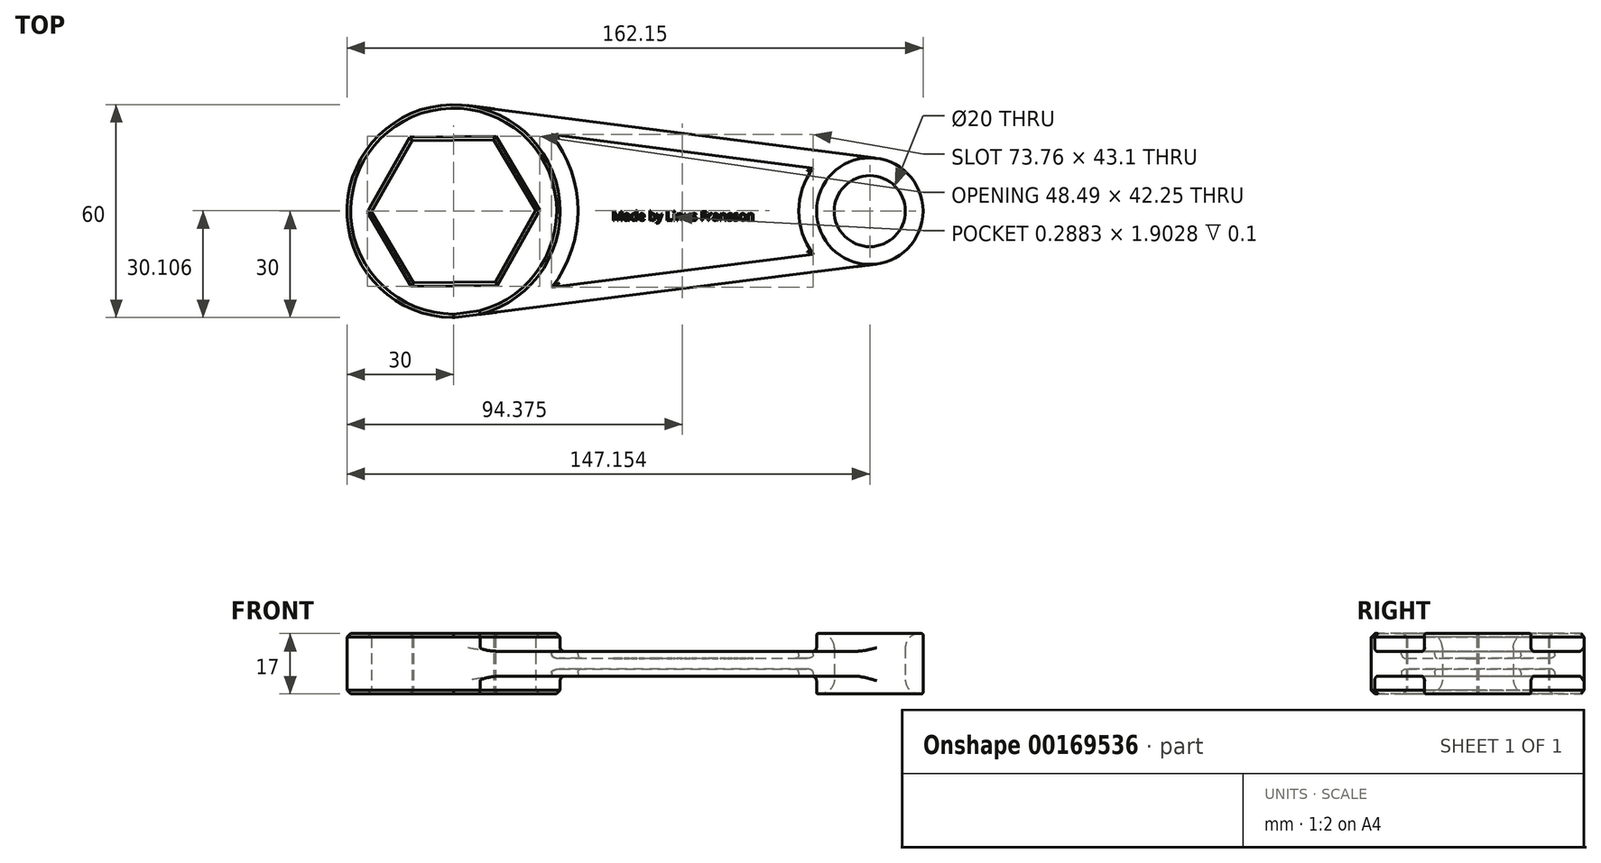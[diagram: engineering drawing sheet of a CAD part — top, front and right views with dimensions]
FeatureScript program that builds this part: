
annotation { "Feature Type Name" : "Feature", "Feature Type Description" : "" }
export const myFeature = defineFeature(function(context is Context, id is Id, definition is map)
    precondition{}
    {
        {
            var Q0;
            Q0=qCreatedBy(makeId("Top.planeOp"),FACE);
            var sketch = newSketch(context, id + "F0", { "sketchPlane" : qUnion([Q0])});
            skCircle(sketch, "E0", {"center": v(0, 0) * mm, "radius": 30 * mm});
            skCircle(sketch, "E1", {"center": v(117.15, 0) * mm, "radius": 15 * mm});
            skCircle(sketch, "E2.cCircle", {"center": v(0, 0) * mm, "radius": 20 * mm, "construction": true});
            skLineSegment(sketch, "E2.0", {"start": v(23.1, 0.24) * mm, "end": v(11.76, -19.88) * mm});
            skLineSegment(sketch, "E2.1", {"start": v(11.76, -19.88) * mm, "end": v(-11.34, -20.12) * mm});
            skLineSegment(sketch, "E2.2", {"start": v(-11.34, -20.12) * mm, "end": v(-23.1, -0.24) * mm});
            skLineSegment(sketch, "E2.3", {"start": v(-23.1, -0.24) * mm, "end": v(-11.76, 19.88) * mm});
            skLineSegment(sketch, "E2.4", {"start": v(-11.76, 19.88) * mm, "end": v(11.34, 20.12) * mm});
            skLineSegment(sketch, "E2.5", {"start": v(11.34, 20.12) * mm, "end": v(23.1, 0.24) * mm});
            skPoint(sketch, "E2.0.midPoint", {"position": v(17.42, -9.82) * mm});
            skCircle(sketch, "E3", {"center": v(117.15, 0) * mm, "radius": 10 * mm});
            skLineSegment(sketch, "E4", {"start": v(119.01, 14.88) * mm, "end": v(0, 30.25) * mm});
            skLineSegment(sketch, "E5", {"start": v(0, -30) * mm, "end": v(119.04, -14.88) * mm});
            skSolve(sketch);
        }
        {
            var Q0;
            {var subQ0=sQuery(id+"F0.wireOp",EDGE,"E4");var subQ1=sQuery(id+"F0.wireOp",EDGE,"E0");var subQ2=makeQuery(id+"F0.imprint","INTERSECT",VERTEX,{"derivedFrom":[subQ1,subQ0]});Q0=makeQuery(id+"F0.imprint","IMPRINT",FACE,{"disambiguationData":[TD([[makeQuery(id+"F0.imprint","IMPRINT",EDGE,{"disambiguationData":[TD([[subQ2,1.0]])],"derivedFrom":subQ1}),-1.0]])]});}
            var Q1;
            Q1=makeQuery(id+"F0.imprint","IMPRINT",FACE,{"disambiguationData":[TD([[makeQuery(id+"F0.imprint","IMPRINT",EDGE,{"derivedFrom":sQuery(id+"F0.wireOp",EDGE,"E2.0")}),1.0]])]});
            var Q2;
            Q2=makeQuery(id+"F0.imprint","IMPRINT",FACE,{"disambiguationData":[TD([[makeQuery(id+"F0.imprint","IMPRINT",EDGE,{"derivedFrom":sQuery(id+"F0.wireOp",EDGE,"E3")}),-1.0]])]});
            extrude(context, id + "F1", {"entities" : qUnion([Q0, Q1, Q2]), "depth" : 7 * mm, "symmetric" : true});
        }
        {
            var Q0;
            Q0=makeQuery(id+"F1.opExtrude","CAP_FACE",FACE,{"disambiguationData":[OSD([sQuery(id+"F0.wireOp",EDGE,"E0"),sQuery(id+"F0.wireOp",EDGE,"E1"),sQuery(id+"F0.wireOp",EDGE,"E2.0"),sQuery(id+"F0.wireOp",EDGE,"E2.1"),sQuery(id+"F0.wireOp",EDGE,"E2.2"),sQuery(id+"F0.wireOp",EDGE,"E2.3"),sQuery(id+"F0.wireOp",EDGE,"E2.4"),sQuery(id+"F0.wireOp",EDGE,"E2.5"),sQuery(id+"F0.wireOp",EDGE,"E3"),sQuery(id+"F0.wireOp",EDGE,"E4"),sQuery(id+"F0.wireOp",EDGE,"E5")])],"isStart":false});
            var sketch = newSketch(context, id + "F2", { "sketchPlane" : qUnion([Q0])});
            skCircle(sketch, "E6", {"center": v(0, 0) * mm, "radius": 30 * mm});
            skCircle(sketch, "E7", {"center": v(117.15, 0) * mm, "radius": 15 * mm});
            skSolve(sketch);
        }
        {
            var Q0;
            Q0=makeQuery(id+"F2.imprint","IMPRINT",FACE,{"disambiguationData":[TD([[makeQuery(id+"F2.imprint","IMPRINT",EDGE,{"derivedFrom":makeQuery(id+"F1.opExtrude","CAP_EDGE",EDGE,{"disambiguationData":[OSD([sQuery(id+"F0.wireOp",EDGE,"E2.0")])],"isStart":false})}),1.0]])]});
            var Q1;
            Q1=makeQuery(id+"F2.imprint","IMPRINT",FACE,{"disambiguationData":[TD([[makeQuery(id+"F2.imprint","IMPRINT",EDGE,{"derivedFrom":makeQuery(id+"F1.opExtrude","CAP_EDGE",EDGE,{"disambiguationData":[OSD([sQuery(id+"F0.wireOp",EDGE,"E3")])],"isStart":false})}),-1.0]])]});
            extrude(context, id + "F3", {"entities" : qUnion([Q0, Q1]), "operationType" : NewBodyOperationType.ADD, "depth" : 5 * mm, "hasSecondDirection" : true, "secondDirectionOppositeDirection" : true, "secondDirectionDepth" : 12 * mm});
        }
        {
            var Q0;
            Q0=makeQuery(id+"F1.opExtrude","CAP_FACE",FACE,{"disambiguationData":[OSD([sQuery(id+"F0.wireOp",EDGE,"E0"),sQuery(id+"F0.wireOp",EDGE,"E1"),sQuery(id+"F0.wireOp",EDGE,"E2.0"),sQuery(id+"F0.wireOp",EDGE,"E2.1"),sQuery(id+"F0.wireOp",EDGE,"E2.2"),sQuery(id+"F0.wireOp",EDGE,"E2.3"),sQuery(id+"F0.wireOp",EDGE,"E2.4"),sQuery(id+"F0.wireOp",EDGE,"E2.5"),sQuery(id+"F0.wireOp",EDGE,"E3"),sQuery(id+"F0.wireOp",EDGE,"E4"),sQuery(id+"F0.wireOp",EDGE,"E5")])],"isStart":false});
            var sketch = newSketch(context, id + "F4", { "sketchPlane" : qUnion([Q0])});
            skCircle(sketch, "E8", {"center": v(0, 0) * mm, "radius": 35 * mm});
            skCircle(sketch, "E9", {"center": v(117.15, 0) * mm, "radius": 20 * mm});
            skLineSegment(sketch, "E10", {"start": v(27.5, 21.66) * mm, "end": v(101.26, 12.14) * mm});
            skLineSegment(sketch, "E11", {"start": v(27.66, -21.45) * mm, "end": v(101.23, -12.1) * mm});
            skSolve(sketch);
        }
        {
            var Q0;
            {var subQ0=sQuery(id+"F4.wireOp",EDGE,"E10");Q0=makeQuery(id+"F4.imprint","IMPRINT",FACE,{"disambiguationData":[TD([[makeQuery(id+"F4.imprint","IMPRINT",EDGE,{"derivedFrom":subQ0}),-1.0]])]});}
            extrude(context, id + "F5", {"entities" : qUnion([Q0]), "operationType" : NewBodyOperationType.REMOVE, "oppositeDirection" : true, "depth" : 2 * mm});
        }
        {
            var Q0;
            Q0=makeQuery(id+"F1.opExtrude","CAP_FACE",FACE,{"disambiguationData":[OSD([sQuery(id+"F0.wireOp",EDGE,"E0"),sQuery(id+"F0.wireOp",EDGE,"E1"),sQuery(id+"F0.wireOp",EDGE,"E2.0"),sQuery(id+"F0.wireOp",EDGE,"E2.1"),sQuery(id+"F0.wireOp",EDGE,"E2.2"),sQuery(id+"F0.wireOp",EDGE,"E2.3"),sQuery(id+"F0.wireOp",EDGE,"E2.4"),sQuery(id+"F0.wireOp",EDGE,"E2.5"),sQuery(id+"F0.wireOp",EDGE,"E3"),sQuery(id+"F0.wireOp",EDGE,"E4"),sQuery(id+"F0.wireOp",EDGE,"E5")])],"isStart":true});
            var sketch = newSketch(context, id + "F6", { "sketchPlane" : qUnion([Q0])});
            skCircle(sketch, "E12", {"center": v(0, 0) * mm, "radius": 35 * mm});
            skCircle(sketch, "E13", {"center": v(117.15, 0) * mm, "radius": 20 * mm});
            skLineSegment(sketch, "E14", {"start": v(27.66, 21.45) * mm, "end": v(101.23, 12.1) * mm});
            skLineSegment(sketch, "E15", {"start": v(101.26, -12.14) * mm, "end": v(27.5, -21.66) * mm});
            skSolve(sketch);
        }
        {
            var Q0;
            {var subQ0=sQuery(id+"F6.wireOp",EDGE,"E14");Q0=makeQuery(id+"F6.imprint","IMPRINT",FACE,{"disambiguationData":[TD([[makeQuery(id+"F6.imprint","IMPRINT",EDGE,{"derivedFrom":subQ0}),-1.0]])]});}
            extrude(context, id + "F7", {"entities" : qUnion([Q0]), "operationType" : NewBodyOperationType.REMOVE, "oppositeDirection" : true, "depth" : 2 * mm});
        }
        {
            var Q0;
            Q0=makeQuery(id+"F3.boolean.opBoolean","INTERSECT",EDGE,{"derivedFrom":[makeQuery(id+"F1.opExtrude","CAP_FACE",FACE,{"disambiguationData":[OSD([sQuery(id+"F0.wireOp",EDGE,"E0"),sQuery(id+"F0.wireOp",EDGE,"E1"),sQuery(id+"F0.wireOp",EDGE,"E2.0"),sQuery(id+"F0.wireOp",EDGE,"E2.1"),sQuery(id+"F0.wireOp",EDGE,"E2.2"),sQuery(id+"F0.wireOp",EDGE,"E2.3"),sQuery(id+"F0.wireOp",EDGE,"E2.4"),sQuery(id+"F0.wireOp",EDGE,"E2.5"),sQuery(id+"F0.wireOp",EDGE,"E3"),sQuery(id+"F0.wireOp",EDGE,"E4"),sQuery(id+"F0.wireOp",EDGE,"E5")])],"isStart":true}),makeQuery(id+"F3.opExtrude","SWEPT_FACE",FACE,{"disambiguationData":[OSD([sQuery(id+"F2.wireOp",EDGE,"E6")])]})]});
            fillet(context, id + "F8", {"entities" : qUnion([Q0]), "radius" : 1.3 * mm, "tangentPropagation" : true, "allowEdgeOverflow" : false});
        }
        {
            var Q0;
            Q0=makeQuery(id+"F7.boolean.opBoolean","COPY",EDGE,{"derivedFrom":makeQuery(id+"F7.opExtrude","CAP_EDGE",EDGE,{"disambiguationData":[OSD([sQuery(id+"F6.wireOp",EDGE,"E14")])],"isStart":false})});
            var Q1;
            Q1=makeQuery(id+"F7.boolean.opBoolean","COPY",EDGE,{"derivedFrom":makeQuery(id+"F7.opExtrude","CAP_EDGE",EDGE,{"disambiguationData":[OSD([sQuery(id+"F6.wireOp",EDGE,"E12")])],"isStart":false})});
            var Q2;
            Q2=makeQuery(id+"F7.boolean.opBoolean","COPY",EDGE,{"derivedFrom":makeQuery(id+"F7.opExtrude","CAP_EDGE",EDGE,{"disambiguationData":[OSD([sQuery(id+"F6.wireOp",EDGE,"E13")])],"isStart":false})});
            var Q3;
            Q3=makeQuery(id+"F7.boolean.opBoolean","COPY",EDGE,{"derivedFrom":makeQuery(id+"F7.opExtrude","CAP_EDGE",EDGE,{"disambiguationData":[OSD([sQuery(id+"F6.wireOp",EDGE,"E15")])],"isStart":false})});
            var Q4;
            Q4=makeQuery(id+"F5.boolean.opBoolean","COPY",EDGE,{"derivedFrom":makeQuery(id+"F5.opExtrude","CAP_EDGE",EDGE,{"disambiguationData":[OSD([sQuery(id+"F4.wireOp",EDGE,"E10")])],"isStart":false})});
            var Q5;
            Q5=makeQuery(id+"F5.boolean.opBoolean","COPY",EDGE,{"derivedFrom":makeQuery(id+"F5.opExtrude","CAP_EDGE",EDGE,{"disambiguationData":[OSD([sQuery(id+"F4.wireOp",EDGE,"E9")])],"isStart":false})});
            var Q6;
            Q6=makeQuery(id+"F5.boolean.opBoolean","COPY",EDGE,{"derivedFrom":makeQuery(id+"F5.opExtrude","CAP_EDGE",EDGE,{"disambiguationData":[OSD([sQuery(id+"F4.wireOp",EDGE,"E11")])],"isStart":false})});
            var Q7;
            Q7=makeQuery(id+"F5.boolean.opBoolean","COPY",EDGE,{"derivedFrom":makeQuery(id+"F5.opExtrude","CAP_EDGE",EDGE,{"disambiguationData":[OSD([sQuery(id+"F4.wireOp",EDGE,"E8")])],"isStart":false})});
            fillet(context, id + "F9", {"entities" : qUnion([Q0, Q1, Q2, Q3, Q4, Q5, Q6, Q7]), "radius" : 1 * mm, "tangentPropagation" : true, "allowEdgeOverflow" : false});
        }
        {
            var Q0;
            Q0=makeQuery(id+"F3.boolean.opBoolean","INTERSECT",EDGE,{"derivedFrom":[makeQuery(id+"F1.opExtrude","CAP_FACE",FACE,{"disambiguationData":[OSD([sQuery(id+"F0.wireOp",EDGE,"E0"),sQuery(id+"F0.wireOp",EDGE,"E1"),sQuery(id+"F0.wireOp",EDGE,"E2.0"),sQuery(id+"F0.wireOp",EDGE,"E2.1"),sQuery(id+"F0.wireOp",EDGE,"E2.2"),sQuery(id+"F0.wireOp",EDGE,"E2.3"),sQuery(id+"F0.wireOp",EDGE,"E2.4"),sQuery(id+"F0.wireOp",EDGE,"E2.5"),sQuery(id+"F0.wireOp",EDGE,"E3"),sQuery(id+"F0.wireOp",EDGE,"E4"),sQuery(id+"F0.wireOp",EDGE,"E5")])],"isStart":true}),makeQuery(id+"F3.opExtrude","SWEPT_FACE",FACE,{"disambiguationData":[OSD([sQuery(id+"F2.wireOp",EDGE,"E7")])]})]});
            fillet(context, id + "F10", {"entities" : qUnion([Q0]), "radius" : 1.3 * mm, "tangentPropagation" : true, "allowEdgeOverflow" : false});
        }
        {
            var Q0;
            Q0=makeQuery(id+"F3.opExtrude","CAP_EDGE",EDGE,{"disambiguationData":[OSD([sQuery(id+"F0.wireOp",EDGE,"E3")])],"isStart":true});
            fillet(context, id + "F11", {"entities" : qUnion([Q0]), "radius" : 4 * mm, "tangentPropagation" : true, "allowEdgeOverflow" : false});
        }
        {
            var Q0;
            Q0=makeQuery(id+"F3.opExtrude","CAP_EDGE",EDGE,{"disambiguationData":[OSD([sQuery(id+"F0.wireOp",EDGE,"E3")])],"isStart":false});
            fillet(context, id + "F12", {"entities" : qUnion([Q0]), "radius" : 4 * mm, "tangentPropagation" : true, "allowEdgeOverflow" : false});
        }
        {
            var Q0;
            Q0=makeQuery(id+"F3.opExtrude","CAP_EDGE",EDGE,{"disambiguationData":[OSD([sQuery(id+"F0.wireOp",EDGE,"E2.3")])],"isStart":true});
            var Q1;
            Q1=makeQuery(id+"F3.opExtrude","CAP_EDGE",EDGE,{"disambiguationData":[OSD([sQuery(id+"F0.wireOp",EDGE,"E2.4")])],"isStart":true});
            var Q2;
            Q2=makeQuery(id+"F3.opExtrude","CAP_EDGE",EDGE,{"disambiguationData":[OSD([sQuery(id+"F0.wireOp",EDGE,"E2.2")])],"isStart":true});
            var Q3;
            Q3=makeQuery(id+"F3.opExtrude","CAP_EDGE",EDGE,{"disambiguationData":[OSD([sQuery(id+"F0.wireOp",EDGE,"E2.5")])],"isStart":true});
            var Q4;
            Q4=makeQuery(id+"F3.opExtrude","CAP_EDGE",EDGE,{"disambiguationData":[OSD([sQuery(id+"F0.wireOp",EDGE,"E2.0")])],"isStart":true});
            var Q5;
            Q5=makeQuery(id+"F3.opExtrude","CAP_FACE",FACE,{"disambiguationData":[OSD([sQuery(id+"F0.wireOp",EDGE,"E2.0"),sQuery(id+"F0.wireOp",EDGE,"E2.1"),sQuery(id+"F0.wireOp",EDGE,"E2.2"),sQuery(id+"F0.wireOp",EDGE,"E2.3"),sQuery(id+"F0.wireOp",EDGE,"E2.4"),sQuery(id+"F0.wireOp",EDGE,"E2.5"),sQuery(id+"F0.wireOp",EDGE,"E5"),sQuery(id+"F2.wireOp",EDGE,"E6")])],"isStart":true});
            var Q6;
            Q6=makeQuery(id+"F3.opExtrude","CAP_FACE",FACE,{"disambiguationData":[OSD([sQuery(id+"F0.wireOp",EDGE,"E2.0"),sQuery(id+"F0.wireOp",EDGE,"E2.1"),sQuery(id+"F0.wireOp",EDGE,"E2.2"),sQuery(id+"F0.wireOp",EDGE,"E2.3"),sQuery(id+"F0.wireOp",EDGE,"E2.4"),sQuery(id+"F0.wireOp",EDGE,"E2.5"),sQuery(id+"F0.wireOp",EDGE,"E5"),sQuery(id+"F2.wireOp",EDGE,"E6")])],"isStart":false});
            chamfer(context, id + "F13", {"entities" : qUnion([Q0, Q1, Q2, Q3, Q4, Q5, Q6]), "width" : 1 * mm, "tangentPropagation" : true});
        }
        {
            var Q0;
            Q0=makeQuery(id+"F3.opExtrude","CAP_EDGE",EDGE,{"disambiguationData":[OSD([sQuery(id+"F2.wireOp",EDGE,"E7")])],"isStart":true});
            var Q1;
            Q1=makeQuery(id+"F3.opExtrude","CAP_EDGE",EDGE,{"disambiguationData":[OSD([sQuery(id+"F2.wireOp",EDGE,"E7")])],"isStart":false});
            fillet(context, id + "F14", {"entities" : qUnion([Q0, Q1]), "radius" : 0.5 * mm, "tangentPropagation" : true, "allowEdgeOverflow" : false});
        }
        {
            var Q0;
            Q0=makeQuery(id+"F3.boolean.opBoolean","INTERSECT",EDGE,{"derivedFrom":[makeQuery(id+"F1.opExtrude","CAP_FACE",FACE,{"disambiguationData":[OSD([sQuery(id+"F0.wireOp",EDGE,"E0"),sQuery(id+"F0.wireOp",EDGE,"E1"),sQuery(id+"F0.wireOp",EDGE,"E2.0"),sQuery(id+"F0.wireOp",EDGE,"E2.1"),sQuery(id+"F0.wireOp",EDGE,"E2.2"),sQuery(id+"F0.wireOp",EDGE,"E2.3"),sQuery(id+"F0.wireOp",EDGE,"E2.4"),sQuery(id+"F0.wireOp",EDGE,"E2.5"),sQuery(id+"F0.wireOp",EDGE,"E3"),sQuery(id+"F0.wireOp",EDGE,"E4"),sQuery(id+"F0.wireOp",EDGE,"E5")])],"isStart":false}),makeQuery(id+"F3.opExtrude","SWEPT_FACE",FACE,{"disambiguationData":[OSD([sQuery(id+"F2.wireOp",EDGE,"E6")])]})]});
            var Q1;
            Q1=makeQuery(id+"F3.boolean.opBoolean","INTERSECT",EDGE,{"derivedFrom":[makeQuery(id+"F1.opExtrude","CAP_FACE",FACE,{"disambiguationData":[OSD([sQuery(id+"F0.wireOp",EDGE,"E0"),sQuery(id+"F0.wireOp",EDGE,"E1"),sQuery(id+"F0.wireOp",EDGE,"E2.0"),sQuery(id+"F0.wireOp",EDGE,"E2.1"),sQuery(id+"F0.wireOp",EDGE,"E2.2"),sQuery(id+"F0.wireOp",EDGE,"E2.3"),sQuery(id+"F0.wireOp",EDGE,"E2.4"),sQuery(id+"F0.wireOp",EDGE,"E2.5"),sQuery(id+"F0.wireOp",EDGE,"E3"),sQuery(id+"F0.wireOp",EDGE,"E4"),sQuery(id+"F0.wireOp",EDGE,"E5")])],"isStart":false}),makeQuery(id+"F3.opExtrude","SWEPT_FACE",FACE,{"disambiguationData":[OSD([sQuery(id+"F2.wireOp",EDGE,"E7")])]})]});
            fillet(context, id + "F15", {"entities" : qUnion([Q0, Q1]), "radius" : 1 * mm, "tangentPropagation" : true, "allowEdgeOverflow" : false});
        }
        {
            var Q0;
            {var subQ0=sQuery(id+"F2.wireOp",EDGE,"E6");var subQ1=sQuery(id+"F0.wireOp",EDGE,"E5");Q0=makeQuery(id+"F3.boolean.opBoolean","MERGE",EDGE,{"derivedFrom":[makeQuery(id+"F1.opExtrude","SWEPT_EDGE",EDGE,{"disambiguationData":[OSD([sQuery(id+"F0.wireOp",EDGE,"E0"),subQ1])]}),makeQuery(id+"F3.opExtrude","SWEPT_EDGE",EDGE,{"disambiguationData":[OSD([subQ1,subQ0]),TDD([makeQuery(id+"F2.imprint","INTERSECT",VERTEX,{"disambiguationData":[OD(0.0)],"derivedFrom":[makeQuery(id+"F1.opExtrude","CAP_EDGE",EDGE,{"disambiguationData":[OSD([subQ1])],"isStart":false}),subQ0]})])]})]});}
            fillet(context, id + "F16", {"entities" : qUnion([Q0]), "radius" : 5 * mm, "tangentPropagation" : true, "allowEdgeOverflow" : false});
        }
        {
            var Q0;
            Q0=makeQuery(id+"F5.boolean.opBoolean","COPY",FACE,{"derivedFrom":makeQuery(id+"F5.opExtrude","CAP_FACE",FACE,{"disambiguationData":[OSD([sQuery(id+"F4.wireOp",EDGE,"E8"),sQuery(id+"F4.wireOp",EDGE,"E9"),sQuery(id+"F4.wireOp",EDGE,"E10"),sQuery(id+"F4.wireOp",EDGE,"E11")])],"isStart":false})});
            var sketch = newSketch(context, id + "F17", { "sketchPlane" : qUnion([Q0])});
            skText(sketch, "E16", { "text": "Made by Linus Fransson", "fontName": "OpenSans-Regular.ttf"});
            const initialGuessF17  = {"E16": [0.04458, -0.0026, 1, 0, 0.00256]};
            skSetInitialGuess(sketch, initialGuessF17);
            skSolve(sketch);
        }
        {
            var Q0;
            Q0 = qSketchRegion(id + "F17", true);
            extrude(context, id + "F18", {"entities" : qUnion([Q0]), "operationType" : NewBodyOperationType.REMOVE, "oppositeDirection" : true, "depth" : 0.1 * mm});
        }
    });
